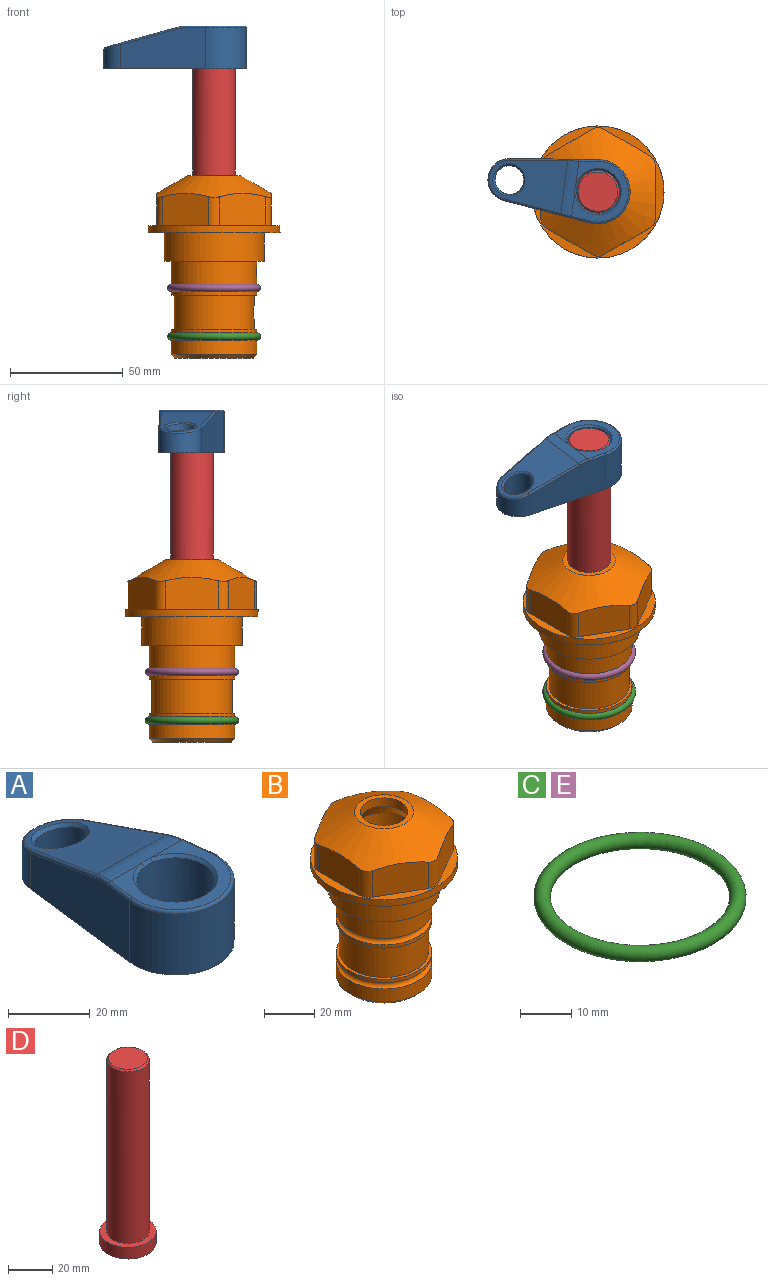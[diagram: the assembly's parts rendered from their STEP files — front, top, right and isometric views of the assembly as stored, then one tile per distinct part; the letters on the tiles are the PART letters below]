
ASSEMBLY  parts=5 mates=4
PART A: 31 faces, bbox 31.7x65.5x19.8 mm
  f0: plane 39.12x18.26mm, normal (0.99,0.12,0), area 612.2mm2, adj f1,f4,f7,f11,f13,f15
  f1: cylinder r=9.53mm len=18.91mm, axis (0,0,-1), area 296.1mm2, adj f0,f2,f7,f17
  f2: plane 39.12x18.26mm, normal (-0.99,0.12,0), area 612.2mm2, adj f1,f4,f7,f12,f14,f16
  f3: cylinder r=6.35mm len=12.7mm, axis (0,0,-1), area 362.4mm2, adj f7,f18
  f4: cylinder r=14.29mm len=28.58mm, axis (0,0,-1), area 882.2mm2, adj f0,f2,f7,f10
  f5: cylinder r=9.53mm len=19.05mm, axis (0,0,-1), area 1092.6mm2, adj f7,f19,f20
  f6: plane 26.99x23.69mm, normal (0,0,1), area 216.2mm2, adj f9,f10,f11,f12,f19
  f7: plane 63.5x28.58mm, normal (0,0,-1), area 661.8mm2, adj f0,f1,f2,f3,f4,f5,f22,f23
  f8: plane 33.52x23.6mm, normal (0,0.26,0.97), area 486mm2, adj f9,f15,f16,f17,f18
  f9: cylinder r=19.05mm len=24.72mm, axis (1,0,0), area 120.4mm2, adj f6,f8,f13,f14,f20
  f10: torus R=13.49mm, axis (0,0,1), area 59mm2, adj f4,f6,f11,f12
  f11: cylinder r=0.79mm len=8.67mm, axis (0.12,-0.99,0), area 10.8mm2, adj f0,f6,f10,f13
  f12: cylinder r=0.79mm len=8.67mm, axis (0.12,0.99,0), area 10.8mm2, adj f2,f6,f10,f14
  f13: bspline ~4.95x1.42mm, area 6.1mm2, adj f0,f9,f11,f15
  f14: bspline ~4.95x1.42mm, area 6.1mm2, adj f2,f9,f12,f16
  f15: cylinder r=0.79mm len=25.95mm, axis (0.12,-0.96,0.26), area 32.9mm2, adj f0,f8,f13,f17
  f16: cylinder r=0.79mm len=25.95mm, axis (0.12,0.96,-0.26), area 32.9mm2, adj f2,f8,f14,f17
  f17: bspline ~18.91x8.38mm, area 30mm2, adj f1,f8,f15,f16
  f18: bspline ~14.29x14.29mm, area 48.3mm2, adj f3,f8
  f19: cone r=9.53mm half-angle=45deg, axis (0,0,1), area 66.5mm2, adj f5,f6,f20
  f20: bspline ~3.22x0.96mm, area 3.5mm2, adj f5,f9,f19
  f21: plane 2.75x2.72mm, normal (0,0,-1), area 2.9mm2, adj f23,f25,f28
  f22: plane 23.05x15.88mm, normal (-0.99,-0.12,0), area 323.6mm2, adj f7,f25,f26,f27,f28,f29
  f23: plane 23.05x15.88mm, normal (0.99,-0.12,0), area 323.6mm2, adj f7,f21,f25,f27,f28,f30
  f24: cylinder r=9.53mm len=10.69mm, axis (0,0,-1), area 114.7mm2, adj f7,f27,f29,f30
  f25: cylinder r=12.7mm len=20.59mm, axis (0,0,-1), area 381.1mm2, adj f7,f21,f22,f23,f26,f28
  f26: plane 2.75x2.72mm, normal (0,0,-1), area 2.9mm2, adj f22,f25,f28
  f27: plane 19.72x18.37mm, normal (0,-0.26,-0.97), area 291.8mm2, adj f22,f23,f24,f28,f29,f30
  f28: cylinder r=15.88mm len=19.92mm, axis (1,0,0), area 54.8mm2, adj f21,f22,f23,f25,f26,f27
  f29: cylinder r=1.59mm len=11mm, axis (0,0,-1), area 34.7mm2, adj f7,f22,f24,f27
  f30: cylinder r=1.59mm len=11mm, axis (0,0,-1), area 34.7mm2, adj f7,f23,f24,f27
PART B: 36 faces, bbox 58.7x58.7x81 mm
  f0: cylinder r=17.78mm len=35.56mm, axis (0,0,1), area 1670.8mm2, adj f23,f24,f31
  f1: cylinder r=19.05mm len=38.1mm, axis (0,0,1), area 1191.9mm2, adj f26,f27,f30
  f2: plane 58.66x58.66mm, normal (0,0,-1), area 1150.6mm2, adj f3,f28
  f3: cylinder r=29.33mm len=58.66mm, axis (0,0,-1), area 585.1mm2, adj f2,f4
  f4: plane 58.66x58.66mm, normal (0,0,1), area 475.9mm2, adj f3,f5,f6,f7,f8,f9,f10,f11
  f5: plane 20.32x14.34mm, normal (-0.5,0.87,0), area 324.4mm2, adj f4,f15,f16,f17
  f6: plane 20.32x14.34mm, normal (0.5,0.87,0), area 324.4mm2, adj f4,f14,f15,f17
  f7: plane 23.48x14.34mm, normal (1,0,0), area 324.4mm2, adj f4,f13,f14,f17
  f8: plane 20.32x14.34mm, normal (0.5,-0.87,0), area 324.4mm2, adj f4,f12,f13,f17
  f9: plane 20.32x14.34mm, normal (-0.5,-0.87,0), area 324.4mm2, adj f4,f11,f12,f17
  f10: plane 23.48x14.34mm, normal (-1,0,0), area 324.4mm2, adj f4,f11,f16,f17
  f11: cylinder r=5.08mm len=12.85mm, axis (0,0,-1), area 67.2mm2, adj f4,f9,f10,f17
  f12: cylinder r=5.08mm len=12.85mm, axis (0,0,-1), area 67.2mm2, adj f4,f8,f9,f17
  f13: cylinder r=5.08mm len=12.85mm, axis (0,0,-1), area 67.2mm2, adj f4,f7,f8,f17
  f14: cylinder r=5.08mm len=12.85mm, axis (0,0,-1), area 67.2mm2, adj f4,f6,f7,f17
  f15: cylinder r=5.08mm len=12.85mm, axis (0,0,-1), area 67.2mm2, adj f4,f5,f6,f17
  f16: cylinder r=5.08mm len=12.85mm, axis (0,0,-1), area 67.2mm2, adj f4,f5,f10,f17
  f17: cone r=11.73mm half-angle=60deg, axis (0,0,-1), area 2071.8mm2, adj f5,f6,f7,f8,f9,f10,f11,f12
  f18: plane 23.46x23.46mm, normal (0,0,1), area 147.4mm2, adj f17,f35
  f19: plane 34.93x34.93mm, normal (0,0,-1), area 958mm2, adj f29
  f20: cylinder r=19.05mm len=38.1mm, axis (0,0,1), area 760.1mm2, adj f21,f29
  f21: torus R=19.05mm, axis (0,0,1), area 565.3mm2, adj f20,f22
  f22: cylinder r=19.05mm len=38.1mm, axis (0,0,1), area 190mm2, adj f21,f23
  f23: plane 38.1x38.1mm, normal (0,0,1), area 146.9mm2, adj f0,f22
  f24: plane 38.1x38.1mm, normal (0,0,-1), area 146.9mm2, adj f0,f25
  f25: cylinder r=19.05mm len=38.1mm, axis (0,0,1), area 190mm2, adj f24,f26
  f26: torus R=19.05mm, axis (0,0,1), area 565.3mm2, adj f1,f25
  f27: plane 44.45x44.45mm, normal (0,0,-1), area 411.7mm2, adj f1,f28
  f28: cylinder r=22.23mm len=44.45mm, axis (0,0,1), area 1773.5mm2, adj f2,f27
  f29: cone r=19.05mm half-angle=45deg, axis (0,0,1), area 257.5mm2, adj f19,f20
  f30: cylinder r=3.17mm len=6.75mm, axis (-1,0,0), area 128mm2, adj f1,f33
  f31: cylinder r=3.17mm len=6.35mm, axis (-1,0,0), area 102.5mm2, adj f0,f33
  f32: plane 25.4x25.4mm, normal (0,0,1), area 506.7mm2, adj f33
  f33: cylinder r=12.7mm len=66.42mm, axis (0,0,-1), area 5236.2mm2, adj f30,f31,f32,f34
  f34: cone r=9.53mm half-angle=30deg, axis (0,0,-1), area 443.4mm2, adj f33,f35
  f35: cylinder r=9.53mm len=19.05mm, axis (0,0,-1), area 240.9mm2, adj f18,f34
PART C: 1 faces, bbox 44.7x44.7x3.2 mm
  f0: torus R=19.05mm, axis (0,0,1), area 1193.9mm2
PART D: 6 faces, bbox 25.4x25.4x101.6 mm
  f0: plane 17.46x17.46mm, normal (0,0,1), area 239.5mm2, adj f5
  f1: plane 25.4x25.4mm, normal (0,0,-1), area 506.7mm2, adj f2
  f2: cylinder r=12.7mm len=25.4mm, axis (0,0,1), area 506.7mm2, adj f1,f3
  f3: plane 25.4x25.4mm, normal (0,0,1), area 221.7mm2, adj f2,f4
  f4: cylinder r=9.53mm len=94.46mm, axis (0,0,1), area 5653mm2, adj f3,f5
  f5: cone r=8.73mm half-angle=45deg, axis (0,0,-1), area 64.4mm2, adj f0,f4
PART E: same geometry as C
PLACE A rot(axis=(0,0,1),82.5deg) t=(0,0,28.35)mm
PLACE B at identity fixed
PLACE C t=(0,0,-21.59)mm
PLACE D rot(axis=(0,0,1),82.5deg) t=(0,0,27.55)mm
PLACE E at identity
MATE cylindrical D.f2 <-> B.f0  axis (0,0,-1) through (0,0,-10.55)mm
MATE fastened C.f0 <-> B.f0  axis (0,0,1) through (0,0,-46.1)mm
MATE fastened A.f4 <-> D.f2  axis (0,0,-1) through (0,0,91.05)mm
MATE fastened E.f0 <-> B.f0  axis (0,0,1) through (0,0,-24.51)mm
